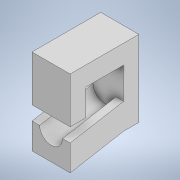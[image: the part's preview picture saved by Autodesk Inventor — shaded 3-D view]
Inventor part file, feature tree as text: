
AUTODESK INVENTOR PART (.ipt)
format: ipt  version: 2021 (Build 250183000, 183)  size: 159,744 bytes
history: native  units: mm
features: sketch x7, extrude x5, plane x1, sweep x1, thread x1
ambient origin geometry x8: Origin, YZ Plane, XZ Plane, XY Plane, X Axis, Y Axis, Z Axis, Center Point
bodies: Solid1 (feature_tree)
feature tree (15):
  extrude  "Extrusion1"  Depth=50.0mm
  extrude  "Extrusion2"  Depth=12.5mm
  extrude  "Extrusion3"  Depth=10.0mm
  extrude  "Extrusion4"  Depth=6.0mm TaperAngle=0.0deg
  extrude  "Extrusion5"  Depth=25.0mm TaperAngle=0.0deg
  sketch  "Sketch6"  dims[d14=25.0mm d15=10.0mm d16=0.0mm d17=15.0mm]
  plane  "Work Plane1"
  sweep  "Sweep1"
  thread  "Thread1"  [1 undecoded]
  sketch  "Sketch1"  dims[d0=25.0mm d1=50.0mm]
  sketch  "Sketch2"  dims[d2=12.5mm d3=12.5mm]
  sketch  "Sketch3"  dims[d4=10.0mm d5=0.0mm d7=3.0mm]
  sketch  "Sketch4"  dims[d8=33.0mm d9=6.0mm d10=0.0mm]
  sketch  "Sketch5"  dims[d11=15.0mm d12=25.0mm d13=0.0mm]
  sketch  "Sketch8"  dims[d18=15.0mm d19=10.0mm d20=0.0mm d21=30.0mm d22=15.0mm d23=17.0mm d24=17.0mm d25=-12.5mm d26=1.745329mm d27=8.5mm d28=0.0mm d29=0.0mm d30=6.0mm d31=0.0mm]
note: 1 required parameter value undecoded (feature->parameter linkage not recoverable at this tier; creation-order binding heuristic only, values carry confidence <= 0.55)
